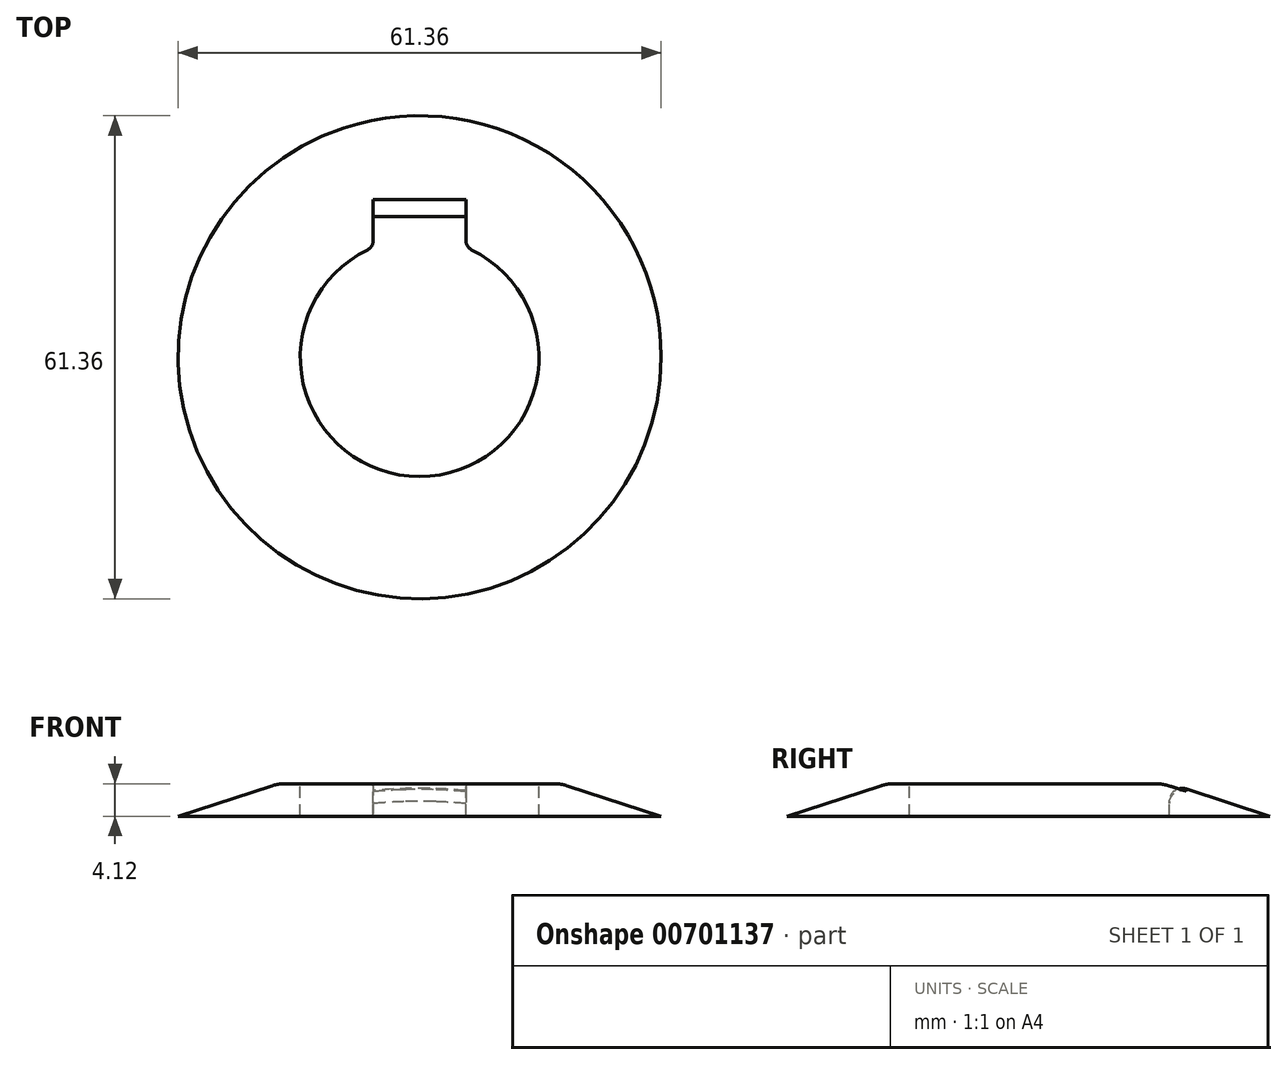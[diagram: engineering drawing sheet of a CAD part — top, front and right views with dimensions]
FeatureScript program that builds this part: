
annotation { "Feature Type Name" : "Feature", "Feature Type Description" : "" }
export const myFeature = defineFeature(function(context is Context, id is Id, definition is map)
    precondition{}
    {
        {
            var Q0;
            Q0=qCreatedBy(makeId("Top.planeOp"),FACE);
            var sketch = newSketch(context, id + "F0", { "sketchPlane" : qUnion([Q0])});
            skCircle(sketch, "E0", {"center": v(0, 0) * mm, "radius": 15.34 * mm});
            skLineSegment(sketch, "E1.bottom", {"start": v(5.9, 17.86) * mm, "end": v(-5.9, 17.86) * mm});
            skLineSegment(sketch, "E1.top", {"start": v(5.9, -3.04) * mm, "end": v(-5.9, -3.04) * mm});
            skLineSegment(sketch, "E1.left", {"start": v(5.9, 17.86) * mm, "end": v(5.9, -3.04) * mm});
            skLineSegment(sketch, "E1.right", {"start": v(-5.9, 17.86) * mm, "end": v(-5.9, -3.04) * mm});
            skPoint(sketch, "E1.middle", {"position": v(0, 7.4) * mm});
            skLineSegment(sketch, "E2.bottom", {"start": v(8.74, -5.45) * mm, "end": v(-9.1, -5.45) * mm});
            skLineSegment(sketch, "E2.top", {"start": v(8.74, 20.98) * mm, "end": v(-9.1, 20.98) * mm});
            skLineSegment(sketch, "E2.left", {"start": v(8.74, -5.45) * mm, "end": v(8.74, 20.98) * mm});
            skLineSegment(sketch, "E2.right", {"start": v(-9.1, -5.45) * mm, "end": v(-9.1, 20.98) * mm});
            skPoint(sketch, "E2.middle", {"position": v(-0.19, 7.77) * mm});
            skCircle(sketch, "E3", {"center": v(0, 0) * mm, "radius": 18.1 * mm});
            skCircle(sketch, "E4", {"center": v(0, 0) * mm, "radius": 30.95 * mm});
            skSolve(sketch);
        }
        {
            var Q0;
            Q0=qCreatedBy(makeId("Front.planeOp"),FACE);
            var sketch = newSketch(context, id + "F1", { "sketchPlane" : qUnion([Q0])});
            skLineSegment(sketch, "E5.bottom", {"start": v(15.16, -2.06) * mm, "end": v(-15.16, -2.06) * mm});
            skLineSegment(sketch, "E5.top", {"start": v(15.16, 2.06) * mm, "end": v(-15.16, 2.06) * mm});
            skLineSegment(sketch, "E5.left", {"start": v(15.16, -2.06) * mm, "end": v(15.16, 2.06) * mm});
            skLineSegment(sketch, "E5.right", {"start": v(-15.16, -2.06) * mm, "end": v(-15.16, 2.06) * mm});
            skPoint(sketch, "E5.middle", {"position": v(0, 0) * mm});
            skLineSegment(sketch, "E6.bottom", {"start": v(17.96, -2.06) * mm, "end": v(-17.96, -2.06) * mm});
            skLineSegment(sketch, "E6.top", {"start": v(17.96, 2.06) * mm, "end": v(-17.96, 2.06) * mm});
            skLineSegment(sketch, "E6.left", {"start": v(17.96, -2.06) * mm, "end": v(17.96, 2.06) * mm});
            skLineSegment(sketch, "E6.right", {"start": v(-17.96, -2.06) * mm, "end": v(-17.96, 2.06) * mm});
            skLineSegment(sketch, "E7", {"start": v(-17.96, -2.06) * mm, "end": v(-30.79, -2.06) * mm});
            skLineSegment(sketch, "E8", {"start": v(-30.79, -2.06) * mm, "end": v(-17.96, 2.06) * mm});
            skLineSegment(sketch, "E9", {"start": v(17.96, -2.06) * mm, "end": v(30.68, -2.06) * mm});
            skLineSegment(sketch, "E10", {"start": v(30.68, -2.06) * mm, "end": v(17.96, 2.06) * mm});
            skLineSegment(sketch, "E11", {"start": v(0, 2.06) * mm, "end": v(0, -2.06) * mm});
            skSolve(sketch);
        }
        {
            var Q0;
            {var subQ0=sQuery(id+"F1.wireOp",EDGE,"E5.left");Q0=makeQuery(id+"F1.imprint","IMPRINT",FACE,{"disambiguationData":[TD([[makeQuery(id+"F1.imprint","IMPRINT",EDGE,{"derivedFrom":subQ0}),-1.0]])]});}
            var Q1;
            Q1=makeQuery(id+"F1.imprint","IMPRINT",FACE,{"disambiguationData":[TD([[makeQuery(id+"F1.imprint","IMPRINT",EDGE,{"derivedFrom":sQuery(id+"F1.wireOp",EDGE,"E6.left")}),-1.0]])]});
            var Q2;
            Q2=sQuery(id+"F1.wireOp",EDGE,"E11");
            revolve(context, id + "F2", {"entities" : qUnion([Q0, Q1]), "axis" : qUnion([Q2]), "revolveType" : RevolveType.FULL});
        }
        {
            var Q0;
            {var subQ1=sQuery(id+"F0.wireOp",EDGE,"E0");var subQ5=sQuery(id+"F0.wireOp",EDGE,"E1.left");var subQ6=makeQuery(id+"F0.imprint","INTERSECT",VERTEX,{"derivedFrom":[subQ1,subQ5]});Q0=makeQuery(id+"F0.imprint","IMPRINT",FACE,{"disambiguationData":[TD([[makeQuery(id+"F0.imprint","IMPRINT",EDGE,{"disambiguationData":[TD([[subQ6,-1.0]])],"derivedFrom":subQ1}),-1.0]])]});}
            var Q1;
            {var subQ0=sQuery(id+"F0.wireOp",EDGE,"E1.right");var subQ1=sQuery(id+"F0.wireOp",EDGE,"E1.bottom");var subQ2=makeQuery(id+"F0.imprint","INTERSECT",VERTEX,{"derivedFrom":[subQ1,subQ0]});Q1=makeQuery(id+"F0.imprint","IMPRINT",FACE,{"disambiguationData":[TD([[makeQuery(id+"F0.imprint","IMPRINT",EDGE,{"disambiguationData":[TD([[subQ2,1.0]])],"derivedFrom":subQ1}),1.0]])]});}
            var Q2;
            {var subQ0=sQuery(id+"F0.wireOp",EDGE,"E1.left");var subQ1=sQuery(id+"F0.wireOp",EDGE,"E1.bottom");var subQ2=makeQuery(id+"F0.imprint","INTERSECT",VERTEX,{"derivedFrom":[subQ1,subQ0]});Q2=makeQuery(id+"F0.imprint","IMPRINT",FACE,{"disambiguationData":[TD([[makeQuery(id+"F0.imprint","IMPRINT",EDGE,{"disambiguationData":[TD([[subQ2,-1.0]])],"derivedFrom":subQ1}),1.0]])]});}
            var Q3;
            {var subQ5=sQuery(id+"F0.wireOp",EDGE,"E1.top");Q3=makeQuery(id+"F0.imprint","IMPRINT",FACE,{"disambiguationData":[TD([[makeQuery(id+"F0.imprint","IMPRINT",EDGE,{"derivedFrom":subQ5}),-1.0]])]});}
            extrude(context, id + "F3", {"entities" : qUnion([Q0, Q1, Q2, Q3]), "operationType" : NewBodyOperationType.REMOVE, "endBound" : BoundingType.SYMMETRIC, "oppositeDirection" : true, "depth" : 25.4 * mm, "offsetDistance" : 25.4 * mm});
        }
        {
            var Q0;
            {var subQ0=sQuery(id+"F1.wireOp",EDGE,"E6.top");var subQ1=sQuery(id+"F1.wireOp",EDGE,"E10");Q0=makeQuery(id+"F3.boolean.opBoolean","SPLIT",EDGE,{"disambiguationData":[TD([makeQuery(id+"F3.opExtrude","SWEPT_FACE",FACE,{"disambiguationData":[OSD([sQuery(id+"F0.wireOp",EDGE,"E1.left")])]})])],"derivedFrom":makeQuery(id+"F2.opRevolve","SWEPT_EDGE",EDGE,{"disambiguationData":[OSD([subQ0,sQuery(id+"F1.wireOp",EDGE,"E6.left"),subQ1])]})});}
            fillet(context, id + "F4", {"entities" : qUnion([Q0]), "radius" : 5.08 * mm, "tangentPropagation" : true, "allowEdgeOverflow" : false});
        }
        {
            var Q0;
            {var subQ0=sQuery(id+"F1.wireOp",EDGE,"E6.top");var subQ1=sQuery(id+"F1.wireOp",EDGE,"E10");Q0=makeQuery(id+"F3.boolean.opBoolean","SPLIT",EDGE,{"disambiguationData":[TD([makeQuery(id+"F3.opExtrude","SWEPT_FACE",FACE,{"disambiguationData":[OSD([sQuery(id+"F0.wireOp",EDGE,"E1.bottom")])]})])],"derivedFrom":makeQuery(id+"F2.opRevolve","SWEPT_EDGE",EDGE,{"disambiguationData":[OSD([subQ0,sQuery(id+"F1.wireOp",EDGE,"E6.left"),subQ1])]})});}
            var Q1;
            Q1=makeQuery(id+"F3.boolean.opBoolean","INTERSECT",EDGE,{"disambiguationData":[OD(0.0)],"derivedFrom":[makeQuery(id+"F2.opRevolve","SWEPT_FACE",FACE,{"disambiguationData":[OSD([sQuery(id+"F1.wireOp",EDGE,"E10")])]}),makeQuery(id+"F3.opExtrude","SWEPT_FACE",FACE,{"disambiguationData":[OSD([sQuery(id+"F0.wireOp",EDGE,"E1.bottom")])]})]});
            var Q2;
            Q2=makeQuery(id+"F3.boolean.opBoolean","INTERSECT",EDGE,{"disambiguationData":[OD(1.0)],"derivedFrom":[makeQuery(id+"F2.opRevolve","SWEPT_FACE",FACE,{"disambiguationData":[OSD([sQuery(id+"F1.wireOp",EDGE,"E10")])]}),makeQuery(id+"F3.opExtrude","SWEPT_FACE",FACE,{"disambiguationData":[OSD([sQuery(id+"F0.wireOp",EDGE,"E1.bottom")])]})]});
            fillet(context, id + "F5", {"entities" : qUnion([Q0, Q1, Q2]), "radius" : 1.65 * mm, "tangentPropagation" : true, "allowEdgeOverflow" : false});
        }
        {
            var Q0;
            Q0=makeQuery(id+"F3.boolean.opBoolean","INTERSECT",EDGE,{"derivedFrom":[makeQuery(id+"F2.opRevolve","SWEPT_FACE",FACE,{"disambiguationData":[OSD([sQuery(id+"F1.wireOp",EDGE,"E5.left")])]}),makeQuery(id+"F3.opExtrude","SWEPT_FACE",FACE,{"disambiguationData":[OSD([sQuery(id+"F0.wireOp",EDGE,"E1.right")])]})]});
            var Q1;
            Q1=makeQuery(id+"F3.boolean.opBoolean","INTERSECT",EDGE,{"derivedFrom":[makeQuery(id+"F2.opRevolve","SWEPT_FACE",FACE,{"disambiguationData":[OSD([sQuery(id+"F1.wireOp",EDGE,"E5.left")])]}),makeQuery(id+"F3.opExtrude","SWEPT_FACE",FACE,{"disambiguationData":[OSD([sQuery(id+"F0.wireOp",EDGE,"E1.left")])]})]});
            fillet(context, id + "F6", {"entities" : qUnion([Q0, Q1]), "radius" : 1.27 * mm, "tangentPropagation" : true, "allowEdgeOverflow" : false});
        }
    });
